# Revit family: IS_Gusto_BD417_BIM_GB
name_source: partatom
category: Plumbing Fixtures
units: mm (PartAtom-declared; Revit-internal decimal feet)

## family parameters
Always vertical = No
Cut with Voids When Loaded = No
OmniClass Number = 23.45.55.17
OmniClass Title = Mixing Faucets
Part Type = Normal
Room Calculation Point = No
Round Connector Dimension = Use Diameter
Shared = No
Work Plane-Based = No

## types (5) — shared parameters
Accessories = https://www.idealstandard.co.uk
AreaUnits = millimetres
AssetType = Fixed
BIMObjectName = IS_IdealStandard_Sinktaps_Gusto_BD417
BIMobject category = Taps & Mixers
BIMobject category code = sanitary-taps-mixers
BIMobject main category = Sanitary
BIMobject main category code = sanitary
Brand = Ideal Standard
Brand url = http://www.idealstandard.co.uk
Category = Taps & Mixers
ConnectionType = Plumbing
CurrencyUnit = £
CurrentRevision = 1
Date of publishing = 19/08/2022
DurationUnit = Years
Edition number = 1
ExpectedLife = 5
FaucetFunction = Sink Mixer
FaucetOperation = Single Lever Sink Mixer
FaucetTopDescription = Single lever
FaucetType = Sink Mixer
GTIN code = https://3800861108849
Help = https://www.idealstandard.co.uk
IFC Classification = Sanitary Terminal
Installation instructions = https://www.idealstandard.co.uk
InstallationInstructions = https://www.idealstandard.co.uk
LinearUnits = millimetres
MaintenanceInformation = https://www.idealstandard.co.uk
Manufacturer = Ideal Standard
Manufacturer name = Ideal Standard
ManufacturerURL = https://www.idealstandard.co.uk
Masterformat 2014 Code = 22 41 16.16
Masterformat 2014 Description = Residential Sink
Material = Brass
Material main = Brass
NBS Reference Code = 45-35-70/345
NBS Reference Description = Water supply fittings for sinks
Name = Sinktaps_Gusto_BD417_IdealStandard
NettWeight = 0.00 Kg
NominalDepth = 264 mm
NominalHeight = 485 mm
NominalLength = 264 mm
NominalWidth = 115 mm
OmniClass Code = 23-31 11 00
OmniClass Description = Faucets
PredefinedType = Taps & Mixers
Product Guid = 5a8c67a4-0456-42e5-8456-4dffdfca1459
Product SKU = BD417
Product certification = https://www.idealstandard.co.uk
Product data url = https://bimobject.com
Product family = Gusto
Product group = Taps & Mixers
Product name = GUSTO SINK MIXER RIM MOUNTED SEMI-PRO BLUE START
Product url = https://www.idealstandard.co.uk
ProductInformation = https://www.idealstandard.co.uk
QR code = http://bimobject.com
Shape = Cylindrical
Size = 115 x 264 x 485 mm
Space = Internal
SpareParts = https://www.idealstandard.co.uk
Technical description = https://www.idealstandard.co.uk
Type Comments = Plumbing
UNSPSC Code = 301815
URL = https://www.idealstandard.co.uk
Uniclass 2015 Code = Pr_40_20_87_82
Uniclass 2015 Name = Sink manual water supply sets
Uniclass2015Code = Pr_40_20_87_84
Uniclass2015Title = Sink taps
Uniclass2015Version = v1.26
Version = 1
VolumeUnits = Liters
WRASURL = https://www.wrasapprovals.co.uk
WarrantyDescription = manufacturer warranty
WarrantyDurationParts = 5
WarrantyDurationUnit = Years
WarrantyStartDate = 19/08/2022
Youtube clip = https://www.youtube.com
zero-valued in all types: Cost, Weight Net (Kg)

## per-type parameters (varying)
| type | BarCode | Color | Description | Features | Finish | MainColor | Model | ModelNumber | ModelReference |
| BD417A5 - Gusto sink mixer rim mounted semi-pro blue start - Magnetic Grey | 3800861109129 | Magnetic Grey | Gusto sink mixer rim mounted semi-pro blue start - Magnetic Grey | Sink mixer rim mounted semi-pro blue start - Magnetic Grey | Magnetic Grey | Magnetic Grey | BD417A5 | BD417A5 | Gusto sink mixer rim mounted semi-pro blue start |
| BD417AA - Gusto sink mixer rim mounted semi-pro blue start - Chrome | 3800861108665 | Chrome | Gusto sink mixer rim mounted semi-pro blue start - Chrome | Sink mixer rim mounted semi-pro blue start - Chrome | Chrome | Chrome | BD417AA | BD417AA | Gusto sink mixer rim mounted semi-pro blue start |
| BD417GN - Gusto sink mixer rm semi-pro blue start - Silver | 3800861108832 | Silver | Gusto sink mixer rm semi-pro blue start - Silver | Sink mixer rm semi-pro blue start - Silver | Silver | Silver | BD417GN | BD417GN | Gusto sink mixer rm semi-pro blue start |
| BD417J4 - Gusto sink mixer rim mounted semi-pro blue start - Brushed Copper | 3800861109280 | Brushed Copper | Gusto sink mixer rim mounted semi-pro blue start - Brushed Copper | Sink mixer rim mounted semi-pro blue start - Brushed Copper | Brushed Copper | Brushed Copper | BD417J4 | BD417J4 | Gusto sink mixer rim mounted semi-pro blue start |
| BD417A2 - Gusto sink mixer rim mounted semi-pro blue start - BrushedGold | 3800861108849 | BrushedGold | Gusto sink mixer rim mounted semi-pro blue start - BrushedGold | Sink mixer rim mounted semi-pro blue start - BrushedGold | BrushedGold | BrushedGold | BD417A2 | BD417A2 | Gusto sink mixer rim mounted semi-pro blue start |

## geometry (parser evidence)
native form markers: Sweep x3
no freeform markers — native parametric forms only
